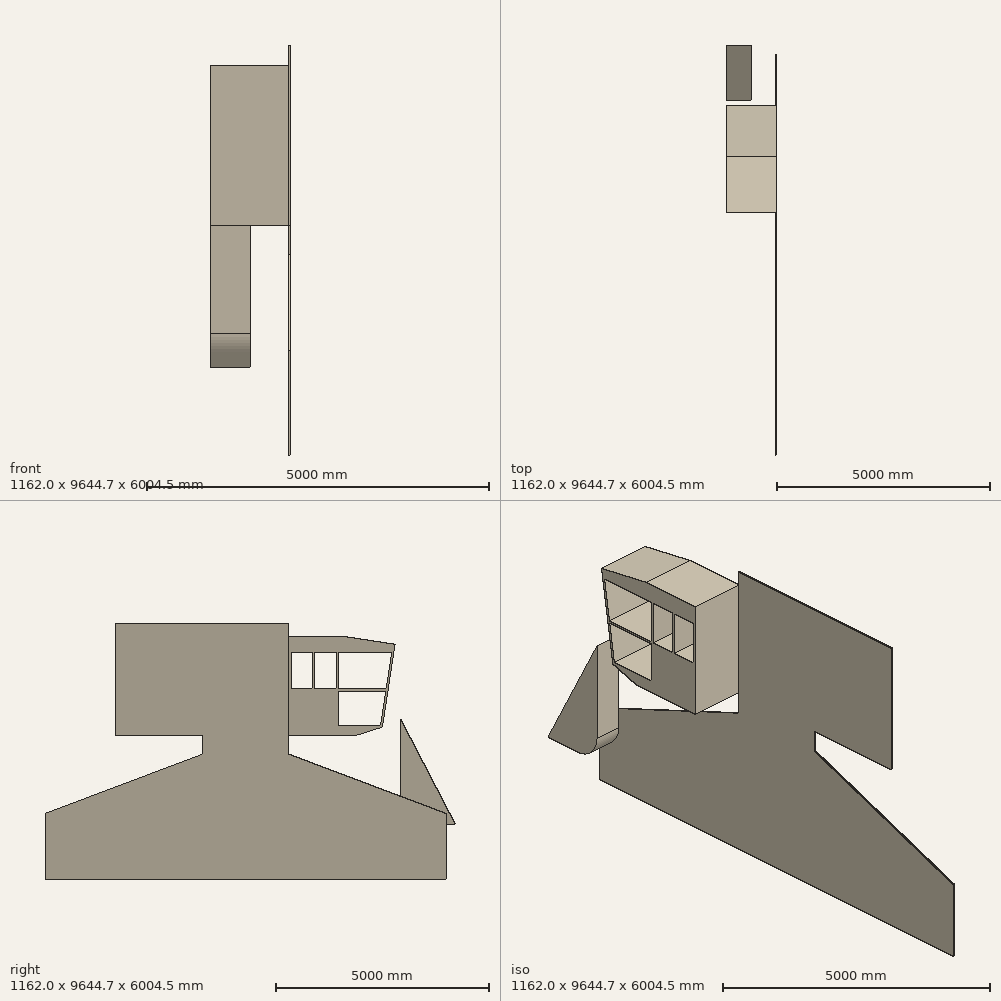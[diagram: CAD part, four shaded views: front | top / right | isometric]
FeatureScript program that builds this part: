
annotation { "Feature Type Name" : "Feature", "Feature Type Description" : "" }
export const myFeature = defineFeature(function(context is Context, id is Id, definition is map)
    precondition{}
    {
        {
            var Q0;
            Q0=qCreatedBy(makeId("Right.planeOp"),FACE);
            var sketch = newSketch(context, id + "F0", { "sketchPlane" : qUnion([Q0])});
            skPoint(sketch, "E0", {"position": v(1500, -2500) * mm});
            skPoint(sketch, "E1", {"position": v(200, 0) * mm});
            skLineSegment(sketch, "E2.bottom", {"start": v(200, 0) * mm, "end": v(1500, 0) * mm});
            skLineSegment(sketch, "E2.top", {"start": v(200, -2500) * mm, "end": v(1500, -2500) * mm});
            skLineSegment(sketch, "E2.left", {"start": v(200, 0) * mm, "end": v(200, -2500) * mm});
            skLineSegment(sketch, "E2.right", {"start": v(1500, 0) * mm, "end": v(1500, -2500) * mm});
            skLineSegment(sketch, "E3", {"start": v(200, 0) * mm, "end": v(1500, -2500) * mm});
            skSolve(sketch);
        }
        {
            var Q0;
            Q0=makeQuery(id+"F0.imprint","IMPRINT",FACE,{"disambiguationData":[TD([[makeQuery(id+"F0.imprint","IMPRINT",EDGE,{"derivedFrom":sQuery(id+"F0.wireOp",EDGE,"E2.top")}),1.0]])]});
            extrude(context, id + "F1", {"entities" : qUnion([Q0]), "offsetDistance" : 25 * mm, "depth" : (2324 / 4) * mm});
        }
        {
            var Q0;
            Q0=makeQuery(id+"F1.opExtrude","SWEPT_EDGE",EDGE,{"disambiguationData":[OSD([sQuery(id+"F0.wireOp",EDGE,"E2.top"),sQuery(id+"F0.wireOp",EDGE,"E2.left")])]});
            fillet(context, id + "F2", {"entities" : qUnion([Q0]), "radius" : 500 * mm, "tangentPropagation" : true, "allowEdgeOverflow" : false});
        }
        {
            var Q0;
            Q0=qCreatedBy(makeId("Right.planeOp"),FACE);
            var sketch = newSketch(context, id + "F3", { "sketchPlane" : qUnion([Q0])});
            skLineSegment(sketch, "E4", {"start": v(-2419, -411.4) * mm, "end": v(-2419, -186.4) * mm});
            skLineSegment(sketch, "E5", {"start": v(-2419, -186.4) * mm, "end": v(-2419, 316.6) * mm});
            skLineSegment(sketch, "E6", {"start": v(-2419, 316.6) * mm, "end": v(-2419, 1816.6) * mm});
            skLineSegment(sketch, "E7", {"start": v(-2419, 1816.6) * mm, "end": v(-2419, 1924.6) * mm});
            skLineSegment(sketch, "E8", {"start": v(-2419, 1924.6) * mm, "end": v(-1119, 1924.6) * mm});
            skLineSegment(sketch, "E9", {"start": v(-1119, 1924.6) * mm, "end": v(81, 1740.11) * mm});
            skLineSegment(sketch, "E10", {"start": v(81, 1740.11) * mm, "end": v(-219.02, -211.4) * mm});
            skLineSegment(sketch, "E11", {"start": v(-219.02, -211.4) * mm, "end": v(-854.1, -411.4) * mm});
            skLineSegment(sketch, "E12", {"start": v(-854.1, -411.4) * mm, "end": v(-2419, -411.4) * mm});
            skSolve(sketch);
        }
        {
            var Q0;
            Q0=makeQuery(id+"F3.imprint","IMPRINT",FACE,{"disambiguationData":[TD([[makeQuery(id+"F3.imprint","IMPRINT",EDGE,{"derivedFrom":sQuery(id+"F3.wireOp",EDGE,"E4")}),-1.0]])]});
            extrude(context, id + "F4", {"entities" : qUnion([Q0]), "depth" : (2324 / 2) * mm, "offsetDistance" : 25 * mm});
        }
        {
            var Q0;
            Q0=makeQuery(id+"F4.opExtrude","CAP_FACE",FACE,{"disambiguationData":[OSD([sQuery(id+"F3.wireOp",EDGE,"E4"),sQuery(id+"F3.wireOp",EDGE,"E5"),sQuery(id+"F3.wireOp",EDGE,"E6"),sQuery(id+"F3.wireOp",EDGE,"E7"),sQuery(id+"F3.wireOp",EDGE,"E8"),sQuery(id+"F3.wireOp",EDGE,"E9"),sQuery(id+"F3.wireOp",EDGE,"E10"),sQuery(id+"F3.wireOp",EDGE,"E11"),sQuery(id+"F3.wireOp",EDGE,"E12")])],"isStart":false});
            var sketch = newSketch(context, id + "F5", { "sketchPlane" : qUnion([Q0])});
            skLineSegment(sketch, "E13", {"start": v(0, 1542.27) * mm, "end": v(-261.92, -161.4) * mm});
            skLineSegment(sketch, "E14", {"start": v(-261.92, -161.4) * mm, "end": v(-1249.98, -161.4) * mm});
            skLineSegment(sketch, "E15", {"start": v(-1249.98, -161.4) * mm, "end": v(-1249.98, 640.43) * mm});
            skLineSegment(sketch, "E16", {"start": v(-1249.98, 1542.27) * mm, "end": v(-1299.98, 1542.27) * mm});
            skLineSegment(sketch, "E17", {"start": v(-1299.98, 1542.27) * mm, "end": v(-1809.49, 1542.27) * mm});
            skLineSegment(sketch, "E18", {"start": v(-1809.49, 1542.27) * mm, "end": v(-1859.49, 1542.27) * mm});
            skLineSegment(sketch, "E19", {"start": v(-1859.49, 1542.27) * mm, "end": v(-2369, 1542.27) * mm});
            skLineSegment(sketch, "E20", {"start": v(-2369, 1542.27) * mm, "end": v(-2419, 1542.27) * mm});
            skLineSegment(sketch, "E21", {"start": v(-138.64, 640.43) * mm, "end": v(-1249.98, 640.43) * mm});
            skLineSegment(sketch, "E22", {"start": v(-130.96, 690.43) * mm, "end": v(-1249.98, 690.43) * mm});
            skLineSegment(sketch, "E23", {"start": v(-2369, 1542.27) * mm, "end": v(-2369, 690.43) * mm});
            skLineSegment(sketch, "E24", {"start": v(-1859.49, 1542.27) * mm, "end": v(-1859.49, 690.43) * mm});
            skLineSegment(sketch, "E25", {"start": v(-1809.49, 1542.27) * mm, "end": v(-1809.49, 690.43) * mm});
            skLineSegment(sketch, "E26", {"start": v(-1299.98, 1542.27) * mm, "end": v(-1299.98, 690.43) * mm});
            skLineSegment(sketch, "E27", {"start": v(0, 1542.27) * mm, "end": v(49.42, 1534.67) * mm, "construction": true});
            skLineSegment(sketch, "E28", {"start": v(-1249.98, 690.43) * mm, "end": v(-1249.98, 1542.27) * mm});
            skLineSegment(sketch, "E29", {"start": v(-1249.98, 640.43) * mm, "end": v(-1249.98, 690.43) * mm});
            skLineSegment(sketch, "E30", {"start": v(-261.92, -161.4) * mm, "end": v(-261.92, -211.4) * mm});
            skLineSegment(sketch, "E31", {"start": v(-1249.98, 690.43) * mm, "end": v(-2369, 690.43) * mm});
            skLineSegment(sketch, "E32", {"start": v(-1249.98, 1542.27) * mm, "end": v(0, 1542.27) * mm});
            skSolve(sketch);
        }
        {
            var Q0;
            Q0=makeQuery(id+"F5.imprint","IMPRINT",FACE,{"disambiguationData":[TD([[makeQuery(id+"F5.imprint","IMPRINT",EDGE,{"derivedFrom":sQuery(id+"F5.wireOp",EDGE,"E19")}),1.0]])]});
            var Q1;
            Q1=makeQuery(id+"F5.imprint","IMPRINT",FACE,{"disambiguationData":[TD([[makeQuery(id+"F5.imprint","IMPRINT",EDGE,{"derivedFrom":sQuery(id+"F5.wireOp",EDGE,"E17")}),1.0]])]});
            var Q2;
            {var subQ2=sQuery(id+"F5.wireOp",EDGE,"E22");Q2=makeQuery(id+"F5.imprint","IMPRINT",FACE,{"disambiguationData":[TD([[makeQuery(id+"F5.imprint","IMPRINT",EDGE,{"derivedFrom":subQ2}),-1.0]])]});}
            var Q3;
            {var subQ0=sQuery(id+"F5.wireOp",EDGE,"E14");Q3=makeQuery(id+"F5.imprint","IMPRINT",FACE,{"disambiguationData":[TD([[makeQuery(id+"F5.imprint","IMPRINT",EDGE,{"derivedFrom":subQ0}),-1.0]])]});}
            extrude(context, id + "F6", {"entities" : qUnion([Q0, Q1, Q2, Q3]), "operationType" : NewBodyOperationType.REMOVE, "endBound" : BoundingType.THROUGH_ALL, "oppositeDirection" : true, "depth" : 25 * mm, "offsetDistance" : 25 * mm});
        }
        {
            var Q0;
            Q0=makeQuery(id+"F4.opExtrude","CAP_FACE",FACE,{"disambiguationData":[OSD([sQuery(id+"F3.wireOp",EDGE,"E4"),sQuery(id+"F3.wireOp",EDGE,"E5"),sQuery(id+"F3.wireOp",EDGE,"E6"),sQuery(id+"F3.wireOp",EDGE,"E7"),sQuery(id+"F3.wireOp",EDGE,"E8"),sQuery(id+"F3.wireOp",EDGE,"E9"),sQuery(id+"F3.wireOp",EDGE,"E10"),sQuery(id+"F3.wireOp",EDGE,"E11"),sQuery(id+"F3.wireOp",EDGE,"E12")])],"isStart":false});
            var sketch = newSketch(context, id + "F7", { "sketchPlane" : qUnion([Q0])});
            skLineSegment(sketch, "E33", {"start": v(-2419, 1924.6) * mm, "end": v(-2419, 2220.85) * mm});
            skLineSegment(sketch, "E34", {"start": v(-2419, 2220.85) * mm, "end": v(-6490.02, 2220.85) * mm});
            skLineSegment(sketch, "E35", {"start": v(-6490.02, 2220.85) * mm, "end": v(-6490.02, -411.4) * mm});
            skLineSegment(sketch, "E36", {"start": v(-6490.02, -411.4) * mm, "end": v(-2419, -411.4) * mm});
            skLineSegment(sketch, "E37", {"start": v(-2419, -411.4) * mm, "end": v(-2419, -844.4) * mm});
            skLineSegment(sketch, "E38", {"start": v(-2419, -844.4) * mm, "end": v(1283.52, -2240.45) * mm});
            skLineSegment(sketch, "E39", {"start": v(1283.52, -2240.45) * mm, "end": v(1283.52, -3783.63) * mm});
            skLineSegment(sketch, "E40", {"start": v(1283.52, -3783.63) * mm, "end": v(-8144.72, -3783.63) * mm});
            skLineSegment(sketch, "E41", {"start": v(-8144.72, -3783.63) * mm, "end": v(-8144.72, -2240.45) * mm});
            skLineSegment(sketch, "E42", {"start": v(-8144.72, -2240.45) * mm, "end": v(-4442.2, -844.4) * mm});
            skLineSegment(sketch, "E43", {"start": v(-4442.2, -844.4) * mm, "end": v(-4442.2, -411.4) * mm});
            skLineSegment(sketch, "E44", {"start": v(-4442.2, -844.4) * mm, "end": v(-4442.2, -2240.45) * mm});
            skLineSegment(sketch, "E45", {"start": v(-4442.2, -2240.45) * mm, "end": v(-8144.72, -2240.45) * mm});
            skLineSegment(sketch, "E46", {"start": v(-2419, -844.4) * mm, "end": v(-2419, -2240.45) * mm});
            skLineSegment(sketch, "E47", {"start": v(-2419, -2240.45) * mm, "end": v(1283.52, -2240.45) * mm});
            skSolve(sketch);
        }
        {
            var Q0;
            Q0=makeQuery(id+"F7.imprint","IMPRINT",FACE,{"disambiguationData":[TD([[makeQuery(id+"F7.imprint","IMPRINT",EDGE,{"derivedFrom":sQuery(id+"F7.wireOp",EDGE,"E33")}),1.0]])]});
            var Q1;
            {var subQ0=sQuery(id+"F7.wireOp",EDGE,"E37");Q1=makeQuery(id+"F7.imprint","IMPRINT",FACE,{"disambiguationData":[TD([[makeQuery(id+"F7.imprint","IMPRINT",EDGE,{"derivedFrom":subQ0}),-1.0]])]});}
            var Q2;
            Q2=makeQuery(id+"F7.imprint","IMPRINT",FACE,{"disambiguationData":[TD([[makeQuery(id+"F7.imprint","IMPRINT",EDGE,{"derivedFrom":sQuery(id+"F7.wireOp",EDGE,"E42")}),-1.0]])]});
            var Q3;
            Q3=makeQuery(id+"F7.imprint","IMPRINT",FACE,{"disambiguationData":[TD([[makeQuery(id+"F7.imprint","IMPRINT",EDGE,{"derivedFrom":sQuery(id+"F7.wireOp",EDGE,"E38")}),-1.0]])]});
            extrude(context, id + "F8", {"entities" : qUnion([Q0, Q1, Q2, Q3]), "oppositeDirection" : true, "depth" : 25 * mm, "offsetDistance" : 25 * mm});
        }
    });
